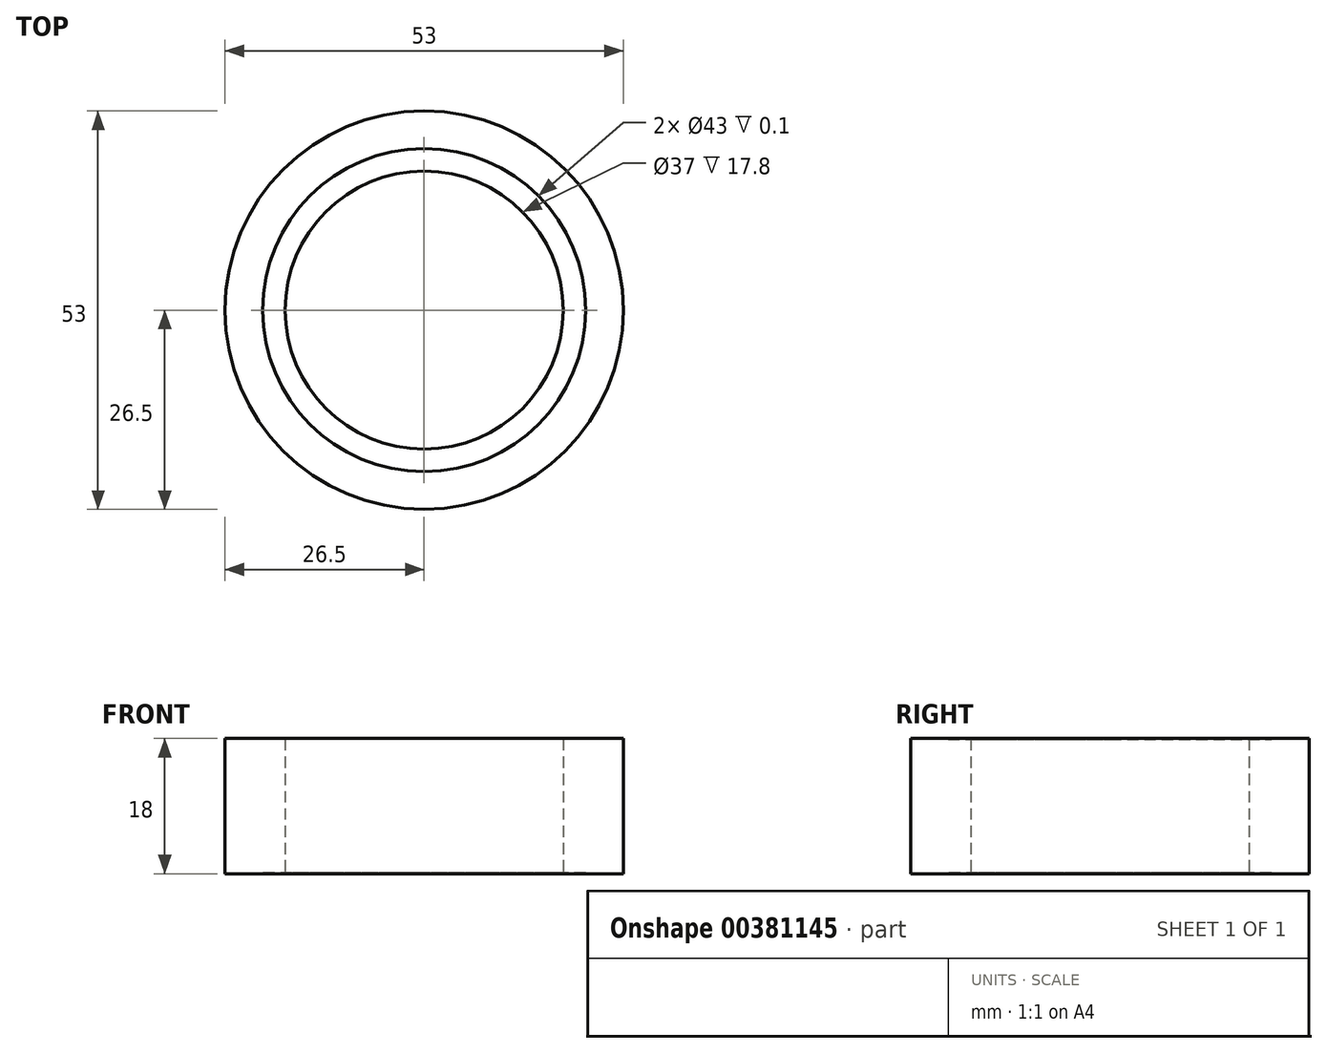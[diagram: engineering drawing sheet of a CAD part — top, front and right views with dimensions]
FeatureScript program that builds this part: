
annotation { "Feature Type Name" : "Feature", "Feature Type Description" : "" }
export const myFeature = defineFeature(function(context is Context, id is Id, definition is map)
    precondition{}
    {
        {
            var Q0;
            Q0=qCreatedBy(makeId("Top.planeOp"),FACE);
            var sketch = newSketch(context, id + "F0", { "sketchPlane" : qUnion([Q0])});
            skCircle(sketch, "E0", {"center": v(0, 0) * mm, "radius": 18.5 * mm});
            skCircle(sketch, "E1", {"center": v(0, 0) * mm, "radius": 21.5 * mm});
            skCircle(sketch, "E2", {"center": v(0, 0) * mm, "radius": 26.5 * mm});
            skSolve(sketch);
        }
        {
            var Q0;
            Q0 = qSketchRegion(id + "F0", true);
            extrude(context, id + "F1", {"entities" : qUnion([Q0]), "endBound" : BoundingType.SYMMETRIC, "depth" : 18 * mm});
        }
        {
            var Q0;
            Q0=makeQuery(id+"F0.imprint","IMPRINT",FACE,{"disambiguationData":[TD([[makeQuery(id+"F0.imprint","IMPRINT",EDGE,{"derivedFrom":sQuery(id+"F0.wireOp",EDGE,"E0")}),-1.0]])]});
            extrude(context, id + "F2", {"entities" : qUnion([Q0]), "operationType" : NewBodyOperationType.ADD, "endBound" : BoundingType.SYMMETRIC, "depth" : 17.8 * mm});
        }
    });
